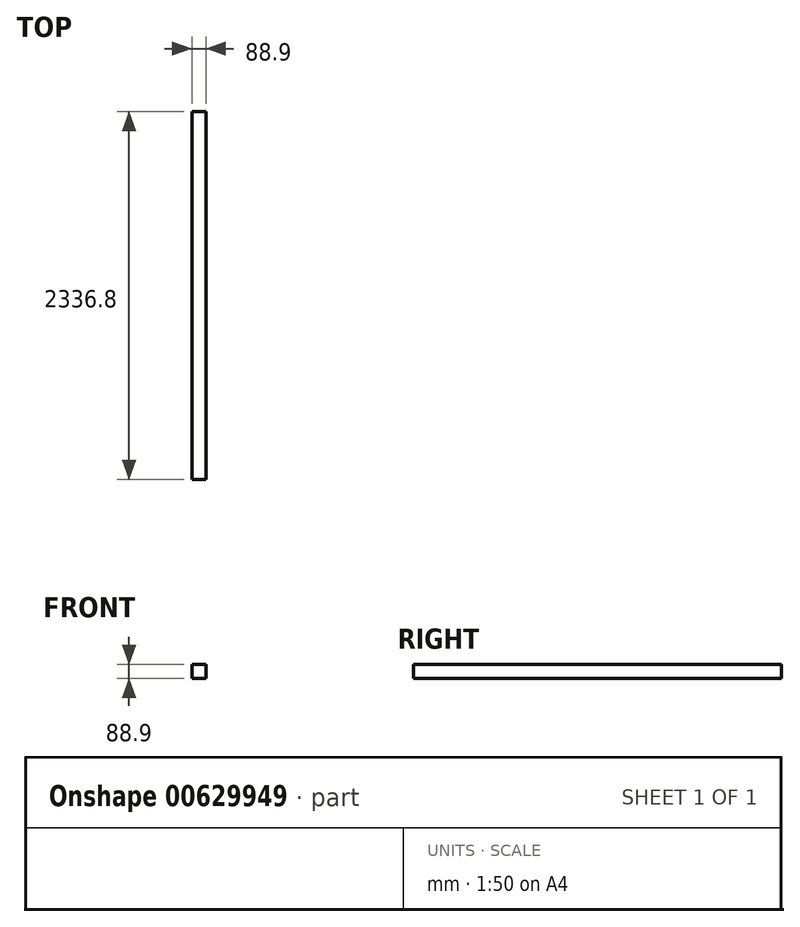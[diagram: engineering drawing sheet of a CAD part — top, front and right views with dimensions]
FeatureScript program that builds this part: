
annotation { "Feature Type Name" : "Feature", "Feature Type Description" : "" }
export const myFeature = defineFeature(function(context is Context, id is Id, definition is map)
    precondition{}
    {
        {
            var Q0;
            Q0=qCreatedBy(makeId("Front.planeOp"),FACE);
            var sketch = newSketch(context, id + "F0", { "sketchPlane" : qUnion([Q0])});
            skLineSegment(sketch, "E0.bottom", {"start": v(-48.39, 71.19) * mm, "end": v(40.51, 71.19) * mm});
            skLineSegment(sketch, "E0.top", {"start": v(-48.39, -17.71) * mm, "end": v(40.51, -17.71) * mm});
            skLineSegment(sketch, "E0.left", {"start": v(-48.39, 71.19) * mm, "end": v(-48.39, -17.71) * mm});
            skLineSegment(sketch, "E0.right", {"start": v(40.51, 71.19) * mm, "end": v(40.51, -17.71) * mm});
            skSolve(sketch);
        }
        {
            var Q0;
            Q0 = qSketchRegion(id + "F0", true);
            extrude(context, id + "F1", {"entities" : qUnion([Q0]), "depth" : 2336.8 * mm, "offsetDistance" : 25.4 * mm});
        }
    });
